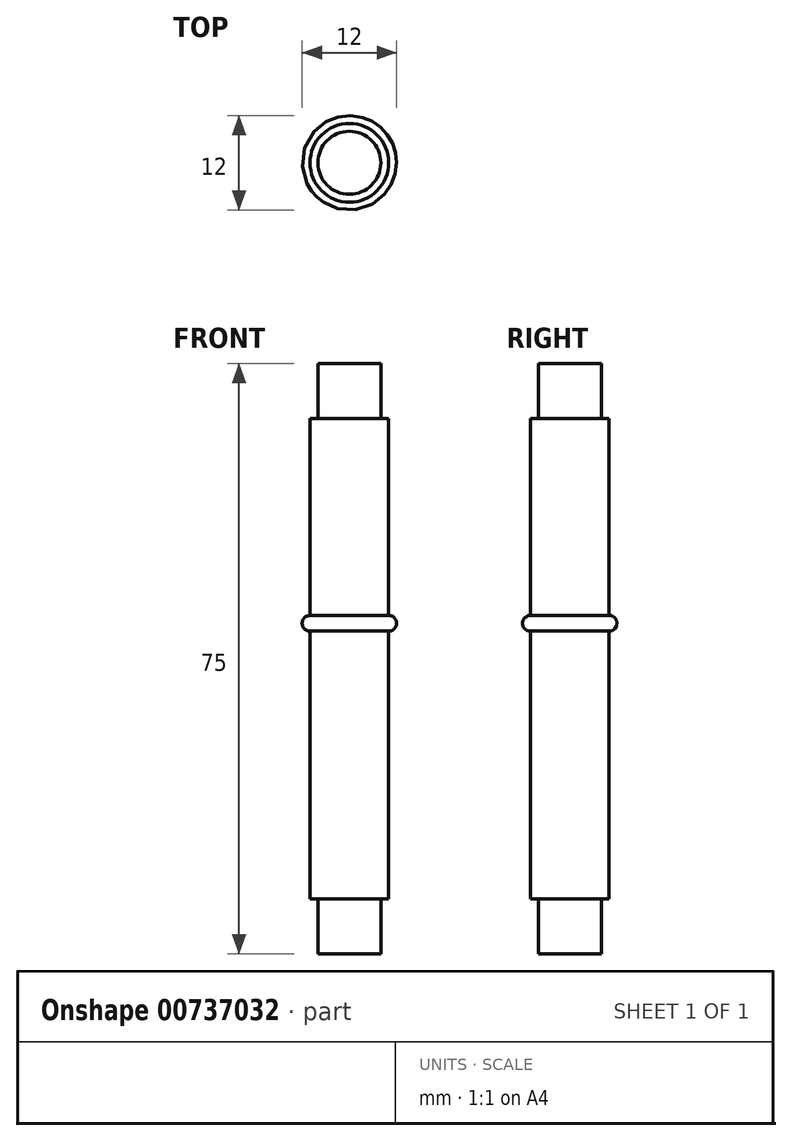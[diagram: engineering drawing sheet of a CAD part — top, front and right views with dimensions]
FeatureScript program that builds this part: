
annotation { "Feature Type Name" : "Feature", "Feature Type Description" : "" }
export const myFeature = defineFeature(function(context is Context, id is Id, definition is map)
    precondition{}
    {
        {
            var Q0;
            Q0=qCreatedBy(makeId("Front.planeOp"),FACE);
            var sketch = newSketch(context, id + "F0", { "sketchPlane" : qUnion([Q0])});
            skLineSegment(sketch, "E0", {"start": v(0, 75) * mm, "end": v(0, 0) * mm});
            skLineSegment(sketch, "E1", {"start": v(0, 0) * mm, "end": v(4, 0) * mm});
            skLineSegment(sketch, "E2", {"start": v(4, 7) * mm, "end": v(4, 0) * mm});
            skLineSegment(sketch, "E3", {"start": v(4, 7) * mm, "end": v(5, 7) * mm});
            skLineSegment(sketch, "E4", {"start": v(5, 7) * mm, "end": v(5, 41) * mm});
            skLineSegment(sketch, "E5", {"start": v(5, 68) * mm, "end": v(4, 68) * mm});
            skLineSegment(sketch, "E6", {"start": v(4, 68) * mm, "end": v(4, 75) * mm});
            skLineSegment(sketch, "E7", {"start": v(4, 75) * mm, "end": v(0, 75) * mm});
            skPoint(sketch, "E8", {"position": v(5, 43) * mm});
            skPoint(sketch, "E9", {"position": v(5, 41) * mm});
            skLineSegment(sketch, "E10.trimOffspring", {"start": v(5, 43) * mm, "end": v(5, 68) * mm});
            skLineSegment(sketch, "E11", {"start": v(5, 41) * mm, "end": v(6, 41) * mm});
            skLineSegment(sketch, "E12", {"start": v(6, 41) * mm, "end": v(6, 43) * mm});
            skLineSegment(sketch, "E13", {"start": v(6, 43) * mm, "end": v(5, 43) * mm});
            skSolve(sketch);
        }
        {
            var Q0;
            Q0 = qSketchRegion(id + "F0", true);
            var Q1;
            Q1=sQuery(id+"F0.wireOp",EDGE,"E0");
            revolve(context, id + "F1", {"surfaceOperationType" : NewSurfaceOperationType.NEW, "entities" : qUnion([Q0]), "axis" : qUnion([Q1]), "revolveType" : RevolveType.FULL});
        }
        {
            var Q0;
            Q0=makeQuery(id+"F1.opRevolve","SWEPT_FACE",FACE,{"disambiguationData":[OSD([sQuery(id+"F0.wireOp",EDGE,"E12")])]});
            fillet(context, id + "F2", {"entities" : qUnion([Q0]), "radius" : 1 * mm, "tangentPropagation" : true, "allowEdgeOverflow" : false});
        }
    });
